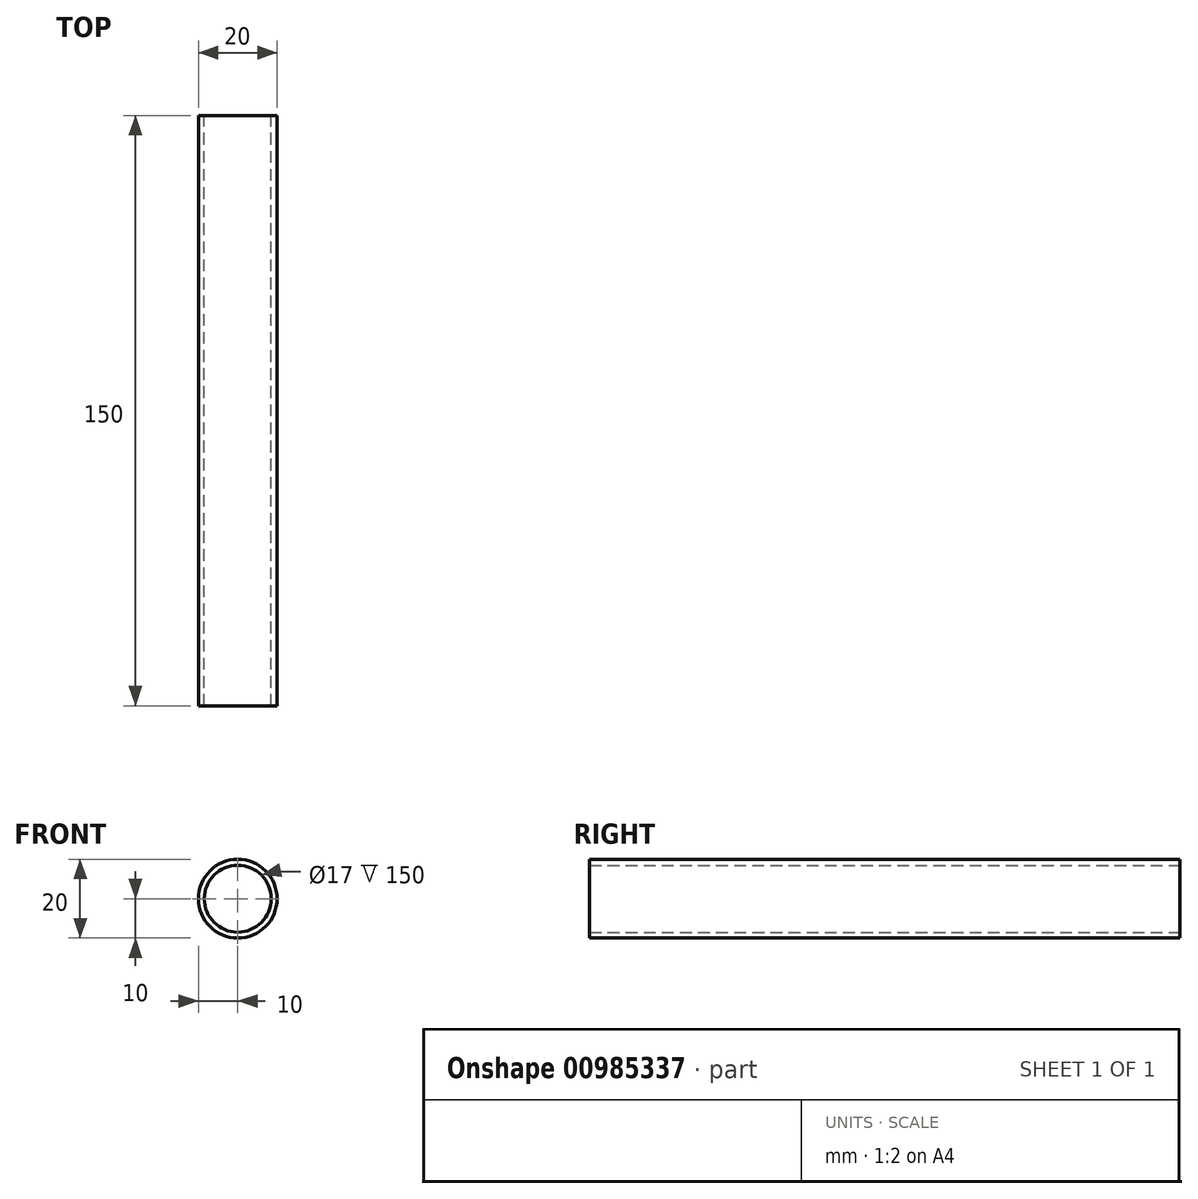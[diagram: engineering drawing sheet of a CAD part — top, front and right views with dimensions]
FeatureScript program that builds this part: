
annotation { "Feature Type Name" : "Feature", "Feature Type Description" : "" }
export const myFeature = defineFeature(function(context is Context, id is Id, definition is map)
    precondition{}
    {
        {
            var Q0;
            Q0=qCreatedBy(makeId("Front.planeOp"),FACE);
            var sketch = newSketch(context, id + "F0", { "sketchPlane" : qUnion([Q0])});
            skCircle(sketch, "E0", {"center": v(0, 0) * mm, "radius": 10 * mm});
            skCircle(sketch, "E1", {"center": v(0, 0) * mm, "radius": 8.5 * mm});
            skSolve(sketch);
        }
        {
            var Q0;
            Q0=makeQuery(id+"F0.imprint","IMPRINT",FACE,{"disambiguationData":[TD([[makeQuery(id+"F0.imprint","IMPRINT",EDGE,{"derivedFrom":sQuery(id+"F0.wireOp",EDGE,"E0")}),1.0]])]});
            var Q1;
            Q1=makeQuery(id+"F0.imprint","IMPRINT",FACE,{"disambiguationData":[TD([[makeQuery(id+"F0.imprint","IMPRINT",EDGE,{"derivedFrom":sQuery(id+"F0.wireOp",EDGE,"df0fa6a2-a233-4493-a15d-55e22b151c3a.1.0")}),1.0]])]});
            var Q2;
            Q2=makeQuery(id+"F0.imprint","IMPRINT",FACE,{"disambiguationData":[TD([[makeQuery(id+"F0.imprint","IMPRINT",EDGE,{"derivedFrom":sQuery(id+"F0.wireOp",EDGE,"df0fa6a2-a233-4493-a15d-55e22b151c3a.2.0")}),1.0]])]});
            var Q3;
            Q3=makeQuery(id+"F0.imprint","IMPRINT",FACE,{"disambiguationData":[TD([[makeQuery(id+"F0.imprint","IMPRINT",EDGE,{"derivedFrom":sQuery(id+"F0.wireOp",EDGE,"df0fa6a2-a233-4493-a15d-55e22b151c3a.3.0")}),1.0]])]});
            var Q4;
            Q4=makeQuery(id+"F0.imprint","IMPRINT",FACE,{"disambiguationData":[TD([[makeQuery(id+"F0.imprint","IMPRINT",EDGE,{"derivedFrom":sQuery(id+"F0.wireOp",EDGE,"df0fa6a2-a233-4493-a15d-55e22b151c3a.4.0")}),1.0]])]});
            var Q5;
            Q5=makeQuery(id+"F0.imprint","IMPRINT",FACE,{"disambiguationData":[TD([[makeQuery(id+"F0.imprint","IMPRINT",EDGE,{"derivedFrom":sQuery(id+"F0.wireOp",EDGE,"df0fa6a2-a233-4493-a15d-55e22b151c3a.5.0")}),1.0]])]});
            extrude(context, id + "F1", {"entities" : qUnion([Q0, Q1, Q2, Q3, Q4, Q5]), "endBound" : BoundingType.SYMMETRIC, "depth" : 150 * mm});
        }
    });
